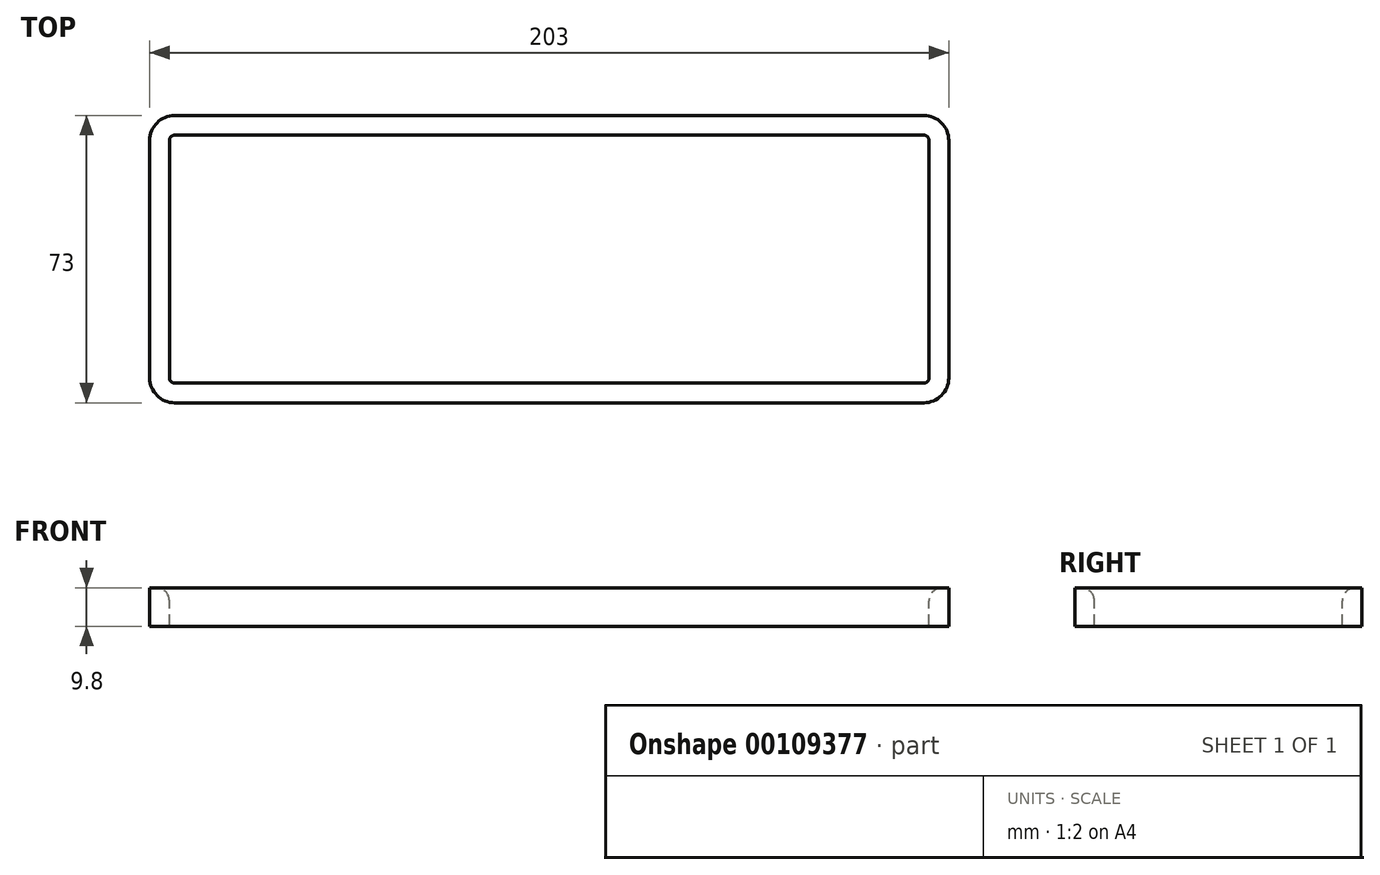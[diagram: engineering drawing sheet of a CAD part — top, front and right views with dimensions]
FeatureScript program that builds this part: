
annotation { "Feature Type Name" : "Feature", "Feature Type Description" : "" }
export const myFeature = defineFeature(function(context is Context, id is Id, definition is map)
    precondition{}
    {
        {
            var Q0;
            Q0=qCreatedBy(makeId("Top.planeOp"),FACE);
            var sketch = newSketch(context, id + "F0", { "sketchPlane" : qUnion([Q0])});
            skLineSegment(sketch, "E0.bottom", {"start": v(-6.35, 0) * mm, "end": v(-196.65, 0) * mm});
            skLineSegment(sketch, "E0.top", {"start": v(-6.35, 73) * mm, "end": v(-196.65, 73) * mm});
            skLineSegment(sketch, "E0.left", {"start": v(0, 6.35) * mm, "end": v(0, 66.65) * mm});
            skLineSegment(sketch, "E0.right", {"start": v(-203, 6.35) * mm, "end": v(-203, 66.65) * mm});
            skPoint(sketch, "E1.visualSharp", {"position": v(0, 73) * mm});
            skArc(sketch, "E1.filletArc", {"start": v(0, 66.65) * mm, "mid": v(-1.86, 71.14) * mm, "end": v(-6.35, 73) * mm});
            skPoint(sketch, "E2.visualSharp", {"position": v(0, 0) * mm});
            skArc(sketch, "E2.filletArc", {"start": v(-6.35, 0) * mm, "mid": v(-1.86, 1.86) * mm, "end": v(0, 6.35) * mm});
            skPoint(sketch, "E3.visualSharp", {"position": v(-203, 0) * mm});
            skArc(sketch, "E3.filletArc", {"start": v(-203, 6.35) * mm, "mid": v(-201.14, 1.86) * mm, "end": v(-196.65, 0) * mm});
            skPoint(sketch, "E4.visualSharp", {"position": v(-203, 73) * mm});
            skArc(sketch, "E4.filletArc", {"start": v(-196.65, 73) * mm, "mid": v(-201.14, 71.14) * mm, "end": v(-203, 66.65) * mm});
            skArc(sketch, "E5.0", {"start": v(-5, 66.65) * mm, "mid": v(-5.4, 67.6) * mm, "end": v(-6.35, 68) * mm});
            skLineSegment(sketch, "E5.1", {"start": v(-5, 6.35) * mm, "end": v(-5, 66.65) * mm});
            skLineSegment(sketch, "E5.2", {"start": v(-6.35, 68) * mm, "end": v(-196.65, 68) * mm});
            skArc(sketch, "E5.3", {"start": v(-6.35, 5) * mm, "mid": v(-5.4, 5.4) * mm, "end": v(-5, 6.35) * mm});
            skArc(sketch, "E5.4", {"start": v(-196.65, 68) * mm, "mid": v(-197.6, 67.6) * mm, "end": v(-198, 66.65) * mm});
            skLineSegment(sketch, "E5.5", {"start": v(-198, 6.35) * mm, "end": v(-198, 66.65) * mm});
            skArc(sketch, "E5.6", {"start": v(-198, 6.35) * mm, "mid": v(-197.6, 5.4) * mm, "end": v(-196.65, 5) * mm});
            skLineSegment(sketch, "E5.7", {"start": v(-6.35, 5) * mm, "end": v(-196.65, 5) * mm});
            skSolve(sketch);
        }
        {
            var Q0;
            Q0=makeQuery(id+"F0.imprint","IMPRINT",FACE,{"disambiguationData":[TD([[makeQuery(id+"F0.imprint","IMPRINT",EDGE,{"derivedFrom":sQuery(id+"F0.wireOp",EDGE,"E0.bottom")}),-1.0]])]});
            extrude(context, id + "F1", {"entities" : qUnion([Q0]), "oppositeDirection" : true, "depth" : 9.8 * mm});
        }
        {
            var Q0;
            Q0=makeQuery(id+"F1.opExtrude","CAP_EDGE",EDGE,{"disambiguationData":[OSD([sQuery(id+"F0.wireOp",EDGE,"E5.2")])],"isStart":true});
            fillet(context, id + "F2", {"entities" : qUnion([Q0]), "radius" : 3.3 * mm, "tangentPropagation" : true, "allowEdgeOverflow" : false});
        }
    });
